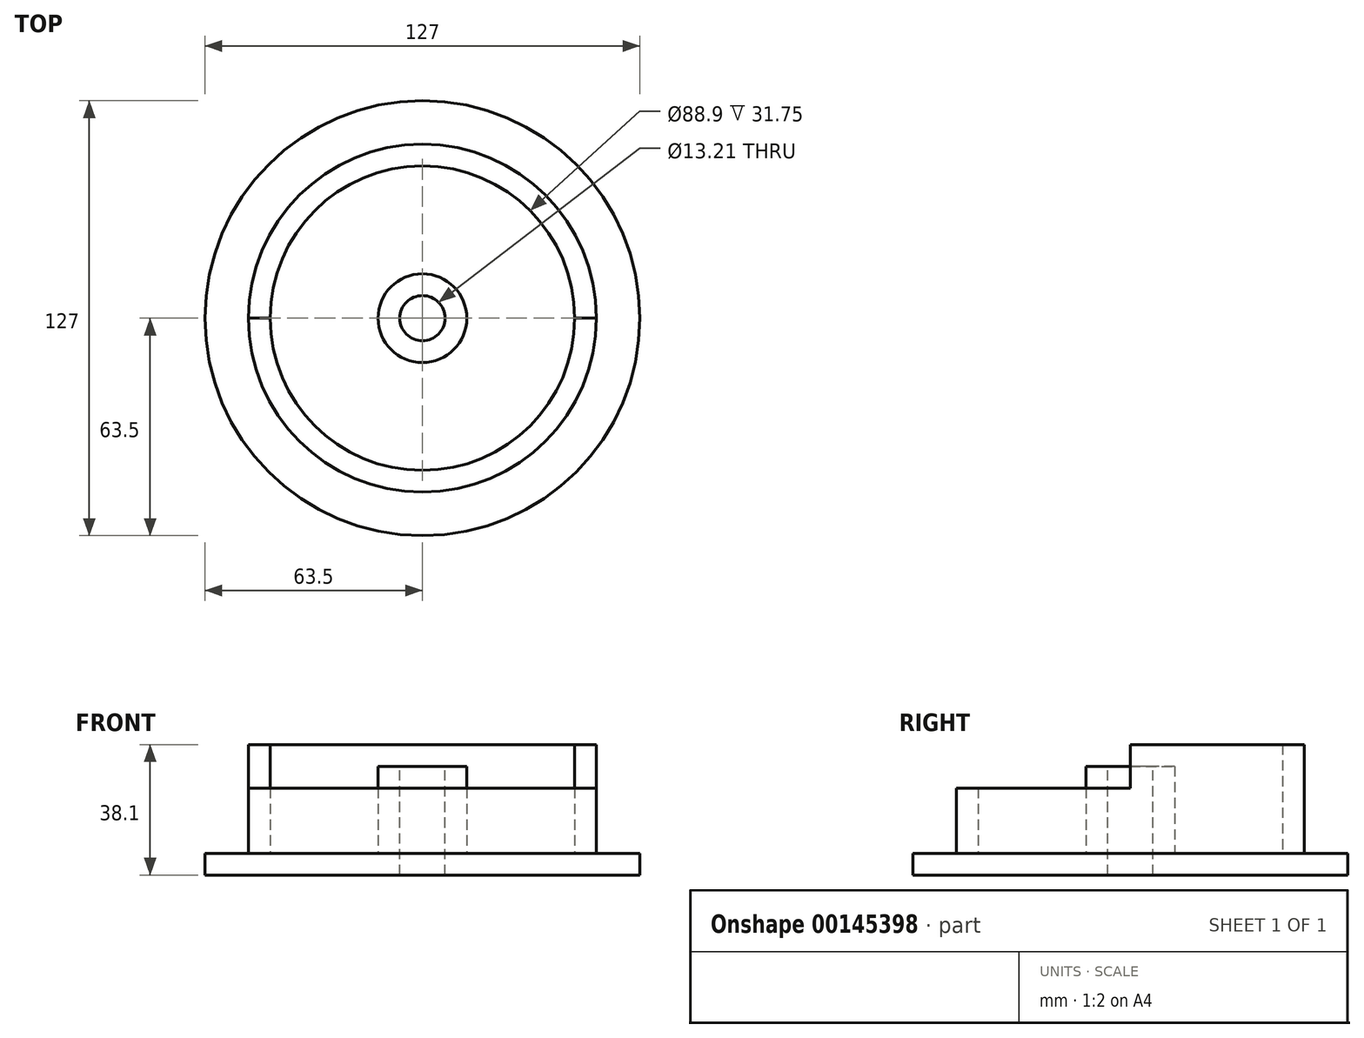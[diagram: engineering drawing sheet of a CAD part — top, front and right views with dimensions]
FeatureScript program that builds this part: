
annotation { "Feature Type Name" : "Feature", "Feature Type Description" : "" }
export const myFeature = defineFeature(function(context is Context, id is Id, definition is map)
    precondition{}
    {
        {
            var Q0;
            Q0=qCreatedBy(makeId("Top.planeOp"),FACE);
            var sketch = newSketch(context, id + "F0", { "sketchPlane" : qUnion([Q0])});
            skCircle(sketch, "E0.0", {"center": v(0, 0) * mm, "radius": 44.45 * mm});
            skCircle(sketch, "E1.0", {"center": v(0, 0) * mm, "radius": 63.5 * mm});
            skCircle(sketch, "E2", {"center": v(0, 0) * mm, "radius": 6.6 * mm});
            skCircle(sketch, "E3.0", {"center": v(0, 0) * mm, "radius": 12.95 * mm});
            skCircle(sketch, "E4.0", {"center": v(0, 0) * mm, "radius": 50.8 * mm});
            skSolve(sketch);
        }
        {
            var Q0;
            Q0=makeQuery(id+"F0.imprint","IMPRINT",FACE,{"disambiguationData":[TD([[makeQuery(id+"F0.imprint","IMPRINT",EDGE,{"derivedFrom":sQuery(id+"F0.wireOp",EDGE,"E1.0")}),1.0]])]});
            var Q1;
            Q1=makeQuery(id+"F0.imprint","IMPRINT",FACE,{"disambiguationData":[TD([[makeQuery(id+"F0.imprint","IMPRINT",EDGE,{"derivedFrom":sQuery(id+"F0.wireOp",EDGE,"E0.0")}),-1.0]])]});
            var Q2;
            Q2=makeQuery(id+"F0.imprint","IMPRINT",FACE,{"disambiguationData":[TD([[makeQuery(id+"F0.imprint","IMPRINT",EDGE,{"derivedFrom":sQuery(id+"F0.wireOp",EDGE,"E0.0")}),1.0]])]});
            var Q3;
            Q3=makeQuery(id+"F0.imprint","IMPRINT",FACE,{"disambiguationData":[TD([[makeQuery(id+"F0.imprint","IMPRINT",EDGE,{"derivedFrom":sQuery(id+"F0.wireOp",EDGE,"E2")}),-1.0]])]});
            extrude(context, id + "F1", {"entities" : qUnion([Q0, Q1, Q2, Q3]), "oppositeDirection" : true, "depth" : 6.35 * mm});
        }
        {
            var Q0;
            Q0=makeQuery(id+"F0.imprint","IMPRINT",FACE,{"disambiguationData":[TD([[makeQuery(id+"F0.imprint","IMPRINT",EDGE,{"derivedFrom":sQuery(id+"F0.wireOp",EDGE,"E0.0")}),-1.0]])]});
            var Q1;
            Q1=makeQuery(id+"F0.imprint","IMPRINT",FACE,{"disambiguationData":[TD([[makeQuery(id+"F0.imprint","IMPRINT",EDGE,{"derivedFrom":sQuery(id+"F0.wireOp",EDGE,"E2")}),-1.0]])]});
            extrude(context, id + "F2", {"entities" : qUnion([Q0, Q1]), "operationType" : NewBodyOperationType.ADD, "depth" : 25.4 * mm});
        }
        {
            var Q0;
            Q0=makeQuery(id+"F2.opExtrude","CAP_FACE",FACE,{"disambiguationData":[OSD([sQuery(id+"F0.wireOp",EDGE,"E0.0"),sQuery(id+"F0.wireOp",EDGE,"E4.0")])],"isStart":false});
            var sketch = newSketch(context, id + "F3", { "sketchPlane" : qUnion([Q0])});
            skLineSegment(sketch, "E5", {"start": v(-50.8, 0) * mm, "end": v(-44.45, 0) * mm});
            skLineSegment(sketch, "E6", {"start": v(44.45, 0) * mm, "end": v(50.8, 0) * mm});
            skSolve(sketch);
        }
        {
            var Q0;
            {var subQ0=sQuery(id+"F3.wireOp",EDGE,"E5");Q0=makeQuery(id+"F3.imprint","IMPRINT",FACE,{"disambiguationData":[TD([[makeQuery(id+"F3.imprint","IMPRINT",EDGE,{"derivedFrom":subQ0}),1.0]])]});}
            extrude(context, id + "F4", {"entities" : qUnion([Q0]), "operationType" : NewBodyOperationType.ADD, "depth" : 6.35 * mm});
        }
        {
            var Q0;
            Q0=makeQuery(id+"F2.opExtrude","CAP_FACE",FACE,{"disambiguationData":[OSD([sQuery(id+"F0.wireOp",EDGE,"E0.0"),sQuery(id+"F0.wireOp",EDGE,"E4.0")])],"isStart":false});
            extrude(context, id + "F5", {"entities" : qUnion([Q0]), "operationType" : NewBodyOperationType.REMOVE, "oppositeDirection" : true, "depth" : 6.35 * mm});
        }
    });
